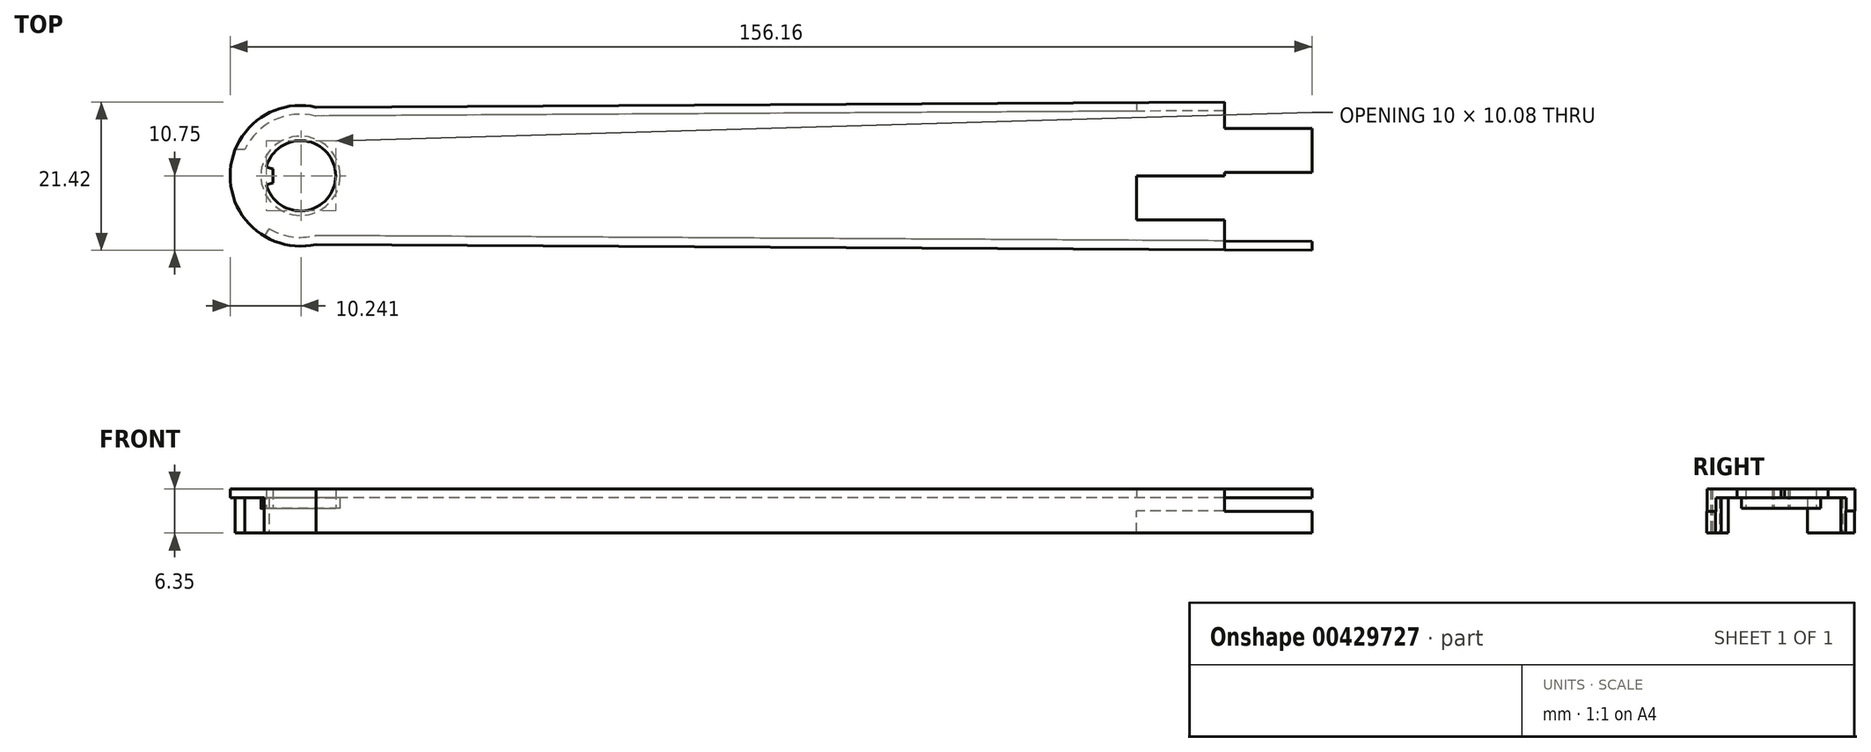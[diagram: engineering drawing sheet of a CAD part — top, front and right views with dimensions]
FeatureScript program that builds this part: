
annotation { "Feature Type Name" : "Feature", "Feature Type Description" : "" }
export const myFeature = defineFeature(function(context is Context, id is Id, definition is map)
    precondition{}
    {
        {
            var Q0;
            Q0=qCreatedBy(makeId("Top.planeOp"),FACE);
            var sketch = newSketch(context, id + "F0", { "sketchPlane" : qUnion([Q0])});
            skPoint(sketch, "E0", {"position": v(-133.35, 0) * mm});
            skPoint(sketch, "E1", {"position": v(133.35, 0) * mm});
            skCircle(sketch, "E2", {"center": v(-133.35, 0) * mm, "radius": 10.16 * mm});
            skCircle(sketch, "E3", {"center": v(133.35, 0) * mm, "radius": 12.07 * mm});
            skPoint(sketch, "E4", {"position": v(129.49, 11.43) * mm});
            skPoint(sketch, "E5", {"position": v(129.49, -11.43) * mm});
            skPoint(sketch, "E6", {"position": v(-131.1, 9.9) * mm});
            skPoint(sketch, "E7", {"position": v(-131.1, -9.9) * mm});
            skPoint(sketch, "E8", {"position": v(-133.35, 10.16) * mm});
            skPoint(sketch, "E9", {"position": v(133.35, 12.07) * mm});
            skLineSegment(sketch, "E10", {"start": v(129.49, 11.43) * mm, "end": v(-131.1, 9.9) * mm});
            skLineSegment(sketch, "E11", {"start": v(129.49, -11.43) * mm, "end": v(-131.1, -9.9) * mm});
            skLineSegment(sketch, "E12", {"start": v(0, 0) * mm, "end": v(0, -10.67) * mm});
            skLineSegment(sketch, "E13", {"start": v(0, 10.67) * mm, "end": v(0, 0) * mm});
            skSolve(sketch);
        }
        {
            var Q0;
            {var subQ0=sQuery(id+"F0.wireOp",EDGE,"E12");Q0=makeQuery(id+"F0.imprint","IMPRINT",FACE,{"disambiguationData":[TD([[makeQuery(id+"F0.imprint","IMPRINT",EDGE,{"derivedFrom":subQ0}),-1.0]])]});}
            var Q1;
            {var subQ0=sQuery(id+"F0.wireOp",EDGE,"E2");var subQ1=makeQuery(id+"F0.imprint","INTERSECT",VERTEX,{"derivedFrom":[subQ0,sQuery(id+"F0.wireOp",EDGE,"E10")]});Q1=makeQuery(id+"F0.imprint","IMPRINT",FACE,{"disambiguationData":[TD([[makeQuery(id+"F0.imprint","IMPRINT",EDGE,{"disambiguationData":[TD([[subQ1,-1.0]])],"derivedFrom":subQ0}),1.0]])]});}
            extrude(context, id + "F1", {"entities" : qUnion([Q0, Q1]), "depth" : 6.35 * mm});
        }
        {
            var Q0;
            Q0=makeQuery(id+"F1.opExtrude","CAP_FACE",FACE,{"disambiguationData":[OSD([sQuery(id+"F0.wireOp",EDGE,"E2"),sQuery(id+"F0.wireOp",EDGE,"E10"),sQuery(id+"F0.wireOp",EDGE,"E11"),sQuery(id+"F0.wireOp",EDGE,"E12"),sQuery(id+"F0.wireOp",EDGE,"E13")])],"isStart":true});
            var Q1;
            Q1=makeQuery(id+"F1.opExtrude","SWEPT_FACE",FACE,{"disambiguationData":[OSD([sQuery(id+"F0.wireOp",EDGE,"E12"),sQuery(id+"F0.wireOp",EDGE,"E13")])]});
            shell(context, id + "F2", {"entities" : qUnion([Q0, Q1]), "thickness" : 1.27 * mm});
        }
        {
            var Q0;
            Q0=makeQuery(id+"F2.opShell","OFFSET_FACE",FACE,{"disambiguationData":[OSD([sQuery(id+"F0.wireOp",EDGE,"E2"),sQuery(id+"F0.wireOp",EDGE,"E10"),sQuery(id+"F0.wireOp",EDGE,"E11"),sQuery(id+"F0.wireOp",EDGE,"ZJ3wcAUT-PQun-HVly-DXgm-6mWhBUt6tBkn"),sQuery(id+"F0.wireOp",EDGE,"E12")])]});
            var sketch = newSketch(context, id + "F3", { "sketchPlane" : qUnion([Q0])});
            skPoint(sketch, "E14", {"position": v(0, -0.5) * mm});
            skLineSegment(sketch, "E15.bottom", {"start": v(0, -0.5) * mm, "end": v(12.65, -0.5) * mm});
            skLineSegment(sketch, "E15.top", {"start": v(0, -6.8) * mm, "end": v(12.65, -6.8) * mm});
            skLineSegment(sketch, "E15.left", {"start": v(0, -0.5) * mm, "end": v(0, -6.8) * mm});
            skLineSegment(sketch, "E15.right", {"start": v(12.65, -0.5) * mm, "end": v(12.65, -6.8) * mm});
            skSolve(sketch);
        }
        {
            var Q0;
            Q0=makeQuery(id+"F3.imprint","IMPRINT",FACE,{"disambiguationData":[TD([[makeQuery(id+"F3.imprint","IMPRINT",EDGE,{"derivedFrom":sQuery(id+"F3.wireOp",EDGE,"E15.bottom")}),-1.0]])]});
            extrude(context, id + "F4", {"entities" : qUnion([Q0]), "oppositeDirection" : true, "depth" : 1.27 * mm});
        }
        {
            var Q0;
            Q0=makeQuery(id+"F4.opExtrude","SWEPT_BODY",BODY,{"disambiguationData":[OSD([sQuery(id+"F3.wireOp",EDGE,"E15.bottom"),sQuery(id+"F3.wireOp",EDGE,"E15.top"),sQuery(id+"F3.wireOp",EDGE,"E15.left"),sQuery(id+"F3.wireOp",EDGE,"E15.right")])]});
            var Q1;
            Q1=makeQuery(id+"F1.opExtrude","SWEPT_BODY",BODY,{"disambiguationData":[OSD([sQuery(id+"F0.wireOp",EDGE,"E2"),sQuery(id+"F0.wireOp",EDGE,"E10"),sQuery(id+"F0.wireOp",EDGE,"E11"),sQuery(id+"F0.wireOp",EDGE,"ZJ3wcAUT-PQun-HVly-DXgm-6mWhBUt6tBkn"),sQuery(id+"F0.wireOp",EDGE,"E12")])]});
            booleanBodies(context, id + "F5", {"operationType" : BooleanOperationType.UNION, "tools" : qUnion([Q0, Q1])});
        }
        {
            var Q0;
            Q0=makeQuery(id+"F2.opShell","OFFSET_FACE",FACE,{"disambiguationData":[OSD([sQuery(id+"F0.wireOp",EDGE,"E11")])]});
            var sketch = newSketch(context, id + "F6", { "sketchPlane" : qUnion([Q0])});
            skLineSegment(sketch, "E16.bottom", {"start": v(0, 0) * mm, "end": v(-12.7, 0) * mm});
            skLineSegment(sketch, "E16.top", {"start": v(0, 3.12) * mm, "end": v(-12.7, 3.12) * mm});
            skLineSegment(sketch, "E16.left", {"start": v(0, 0) * mm, "end": v(0, 3.12) * mm});
            skLineSegment(sketch, "E16.right", {"start": v(-12.7, 0) * mm, "end": v(-12.7, 3.12) * mm});
            skSolve(sketch);
        }
        {
            var Q0;
            {var subQ3=sQuery(id+"F6.wireOp",EDGE,"E16.right");Q0=makeQuery(id+"F6.imprint","IMPRINT",FACE,{"disambiguationData":[TD([[makeQuery(id+"F6.imprint","IMPRINT",EDGE,{"derivedFrom":subQ3}),-1.0]])]});}
            extrude(context, id + "F7", {"entities" : qUnion([Q0]), "operationType" : NewBodyOperationType.ADD, "oppositeDirection" : true, "depth" : 1.27 * mm});
        }
        {
            var Q0;
            Q0=makeQuery(id+"F2.opShell","OFFSET_FACE",FACE,{"disambiguationData":[OSD([sQuery(id+"F0.wireOp",EDGE,"E10")])]});
            var sketch = newSketch(context, id + "F8", { "sketchPlane" : qUnion([Q0])});
            skPoint(sketch, "E17", {"position": v(1.32, 0) * mm});
            skLineSegment(sketch, "E18.bottom", {"start": v(1.32, 0) * mm, "end": v(-12.65, 0) * mm});
            skLineSegment(sketch, "E18.top", {"start": v(1.32, 3.18) * mm, "end": v(-12.65, 3.17) * mm});
            skLineSegment(sketch, "E18.left", {"start": v(1.32, 0) * mm, "end": v(1.32, 3.18) * mm});
            skLineSegment(sketch, "E18.right", {"start": v(-12.65, 0) * mm, "end": v(-12.65, 3.17) * mm});
            skSolve(sketch);
        }
        {
            var Q0;
            {var subQ4=sQuery(id+"F8.wireOp",EDGE,"E18.right");Q0=makeQuery(id+"F8.imprint","IMPRINT",FACE,{"disambiguationData":[TD([[makeQuery(id+"F8.imprint","IMPRINT",EDGE,{"derivedFrom":subQ4}),-1.0]])]});}
            var Q1;
            {var subQ3=sQuery(id+"F8.wireOp",EDGE,"E18.left");Q1=makeQuery(id+"F8.imprint","IMPRINT",FACE,{"disambiguationData":[TD([[makeQuery(id+"F8.imprint","IMPRINT",EDGE,{"derivedFrom":subQ3}),1.0]])]});}
            extrude(context, id + "F9", {"entities" : qUnion([Q0, Q1]), "operationType" : NewBodyOperationType.REMOVE, "oppositeDirection" : true, "depth" : 25.4 * mm});
        }
        {
            var Q0;
            Q0=makeQuery(id+"F5.opBoolean","MERGE",FACE,{"derivedFrom":[makeQuery(id+"F2.opShell","OFFSET_FACE",FACE,{"disambiguationData":[OSD([sQuery(id+"F0.wireOp",EDGE,"E2"),sQuery(id+"F0.wireOp",EDGE,"E10"),sQuery(id+"F0.wireOp",EDGE,"E11"),sQuery(id+"F0.wireOp",EDGE,"E12"),sQuery(id+"F0.wireOp",EDGE,"E13")])]}),makeQuery(id+"F4.opExtrude","CAP_FACE",FACE,{"disambiguationData":[OSD([sQuery(id+"F3.wireOp",EDGE,"E15.bottom"),sQuery(id+"F3.wireOp",EDGE,"E15.top"),sQuery(id+"F3.wireOp",EDGE,"E15.left"),sQuery(id+"F3.wireOp",EDGE,"E15.right")])],"isStart":true})]});
            var sketch = newSketch(context, id + "F10", { "sketchPlane" : qUnion([Q0])});
            skCircle(sketch, "E19", {"center": v(-133.35, 0) * mm, "radius": 5.72 * mm});
            skSolve(sketch);
        }
        {
            var Q0;
            Q0=makeQuery(id+"F10.imprint","IMPRINT",FACE,{"disambiguationData":[TD([[makeQuery(id+"F10.imprint","IMPRINT",EDGE,{"derivedFrom":sQuery(id+"F10.wireOp",EDGE,"E19")}),1.0]])]});
            extrude(context, id + "F11", {"entities" : qUnion([Q0]), "operationType" : NewBodyOperationType.ADD, "depth" : 1.52 * mm});
        }
        {
            var Q0;
            Q0=makeQuery(id+"F11.opExtrude","CAP_FACE",FACE,{"disambiguationData":[OSD([sQuery(id+"F10.wireOp",EDGE,"E19")])],"isStart":false});
            var sketch = newSketch(context, id + "F12", { "sketchPlane" : qUnion([Q0])});
            skCircle(sketch, "E20", {"center": v(-133.35, 0) * mm, "radius": 5.08 * mm});
            skPoint(sketch, "E21", {"position": v(-138.27, 1.27) * mm});
            skPoint(sketch, "E22", {"position": v(-138.27, -1.27) * mm});
            skPoint(sketch, "E23", {"position": v(-137.31, 1.02) * mm});
            skPoint(sketch, "E24", {"position": v(-137.31, -1.02) * mm});
            skPoint(sketch, "E25", {"position": v(-139.07, 0) * mm});
            skLineSegment(sketch, "E26", {"start": v(-138.27, 1.27) * mm, "end": v(-137.31, 1.02) * mm});
            skLineSegment(sketch, "E27", {"start": v(-137.31, -1.02) * mm, "end": v(-137.31, 1.02) * mm});
            skLineSegment(sketch, "E28", {"start": v(-137.31, -1.02) * mm, "end": v(-138.27, -1.27) * mm});
            skSolve(sketch);
        }
        {
            var Q0;
            {var subQ0=sQuery(id+"F12.wireOp",EDGE,"E26");Q0=makeQuery(id+"F12.imprint","IMPRINT",FACE,{"disambiguationData":[TD([[makeQuery(id+"F12.imprint","IMPRINT",EDGE,{"derivedFrom":subQ0}),1.0]])]});}
            extrude(context, id + "F13", {"entities" : qUnion([Q0]), "operationType" : NewBodyOperationType.REMOVE, "oppositeDirection" : true, "depth" : 25.4 * mm});
        }
        {
            var Q0;
            Q0=makeQuery(id+"F7.boolean.opBoolean","MERGE",FACE,{"derivedFrom":[makeQuery(id+"F1.opExtrude","CAP_FACE",FACE,{"disambiguationData":[OSD([sQuery(id+"F0.wireOp",EDGE,"E2"),sQuery(id+"F0.wireOp",EDGE,"E10"),sQuery(id+"F0.wireOp",EDGE,"E11"),sQuery(id+"F0.wireOp",EDGE,"E12"),sQuery(id+"F0.wireOp",EDGE,"E13")])],"isStart":true}),makeQuery(id+"F7.opExtrude","SWEPT_FACE",FACE,{"disambiguationData":[OSD([sQuery(id+"F6.wireOp",EDGE,"E16.bottom")])]})]});
            var sketch = newSketch(context, id + "F14", { "sketchPlane" : qUnion([Q0])});
            skPoint(sketch, "E29", {"position": v(-141.38, -3.81) * mm});
            skPoint(sketch, "E30", {"position": v(-137.93, 7.62) * mm});
            skPoint(sketch, "E31", {"position": v(-133.35, 0) * mm});
            skPoint(sketch, "E32", {"position": v(-138.58, 8.7) * mm});
            skPoint(sketch, "E33", {"position": v(-142.77, -3.81) * mm});
            skLineSegment(sketch, "E34", {"start": v(-138.58, 8.7) * mm, "end": v(-133.35, 0) * mm});
            skLineSegment(sketch, "E35", {"start": v(-142.77, -3.81) * mm, "end": v(-141.38, -3.81) * mm});
            skArc(sketch, "E36", {"start": v(-137.93, 7.62) * mm, "mid": v(-141.86, 2.57) * mm, "end": v(-141.38, -3.8) * mm});
            skArc(sketch, "E37", {"start": v(-138.58, 8.7) * mm, "mid": v(-142.99, 3.22) * mm, "end": v(-142.77, -3.81) * mm});
            skSolve(sketch);
        }
        {
            var Q0;
            Q0=makeQuery(id+"F14.imprint","IMPRINT",FACE,{"disambiguationData":[TD([[makeQuery(id+"F14.imprint","IMPRINT",EDGE,{"derivedFrom":sQuery(id+"F14.wireOp",EDGE,"E35")}),1.0]])]});
            var Q1;
            Q1=makeQuery(id+"F5.opBoolean","MERGE",FACE,{"derivedFrom":[makeQuery(id+"F2.opShell","OFFSET_FACE",FACE,{"disambiguationData":[OSD([sQuery(id+"F0.wireOp",EDGE,"E2"),sQuery(id+"F0.wireOp",EDGE,"E10"),sQuery(id+"F0.wireOp",EDGE,"E11"),sQuery(id+"F0.wireOp",EDGE,"E12"),sQuery(id+"F0.wireOp",EDGE,"E13")])]}),makeQuery(id+"F4.opExtrude","CAP_FACE",FACE,{"disambiguationData":[OSD([sQuery(id+"F3.wireOp",EDGE,"E15.bottom"),sQuery(id+"F3.wireOp",EDGE,"E15.top"),sQuery(id+"F3.wireOp",EDGE,"E15.left"),sQuery(id+"F3.wireOp",EDGE,"E15.right")])],"isStart":true})]});
            extrude(context, id + "F15", {"entities" : qUnion([Q0]), "operationType" : NewBodyOperationType.REMOVE, "endBound" : BoundingType.UP_TO_SURFACE, "oppositeDirection" : true, "endBoundEntityFace" : qUnion([Q1]), "depth" : 25.4 * mm});
        }
        {
            var Q0;
            {var subQ0=sQuery(id+"F3.wireOp",EDGE,"E15.right");var subQ1=sQuery(id+"F3.wireOp",EDGE,"E15.left");var subQ2=sQuery(id+"F3.wireOp",EDGE,"E15.top");var subQ3=sQuery(id+"F3.wireOp",EDGE,"E15.bottom");var subQ4=sQuery(id+"F0.wireOp",EDGE,"E13");var subQ5=sQuery(id+"F0.wireOp",EDGE,"E12");var subQ6=sQuery(id+"F0.wireOp",EDGE,"E11");var subQ7=sQuery(id+"F0.wireOp",EDGE,"E10");var subQ8=sQuery(id+"F0.wireOp",EDGE,"E2");Q0=makeQuery(id+"F15.boolean.opBoolean","MERGE",FACE,{"derivedFrom":[makeQuery(id+"F5.opBoolean","MERGE",FACE,{"derivedFrom":[makeQuery(id+"F2.opShell","OFFSET_FACE",FACE,{"disambiguationData":[OSD([subQ8,subQ7,subQ6,subQ5,subQ4])]}),makeQuery(id+"F4.opExtrude","CAP_FACE",FACE,{"disambiguationData":[OSD([subQ3,subQ2,subQ1,subQ0])],"isStart":true})]}),makeQuery(id+"F15.opExtrude","CAP_FACE",FACE,{"disambiguationData":[OSD([subQ8,subQ7,subQ6,subQ5,subQ4,subQ3,subQ2,subQ1,subQ0])],"isStart":false})]});}
            var sketch = newSketch(context, id + "F16", { "sketchPlane" : qUnion([Q0])});
            skLineSegment(sketch, "E38.bottom", {"start": v(0, 0) * mm, "end": v(-12.7, 0) * mm});
            skLineSegment(sketch, "E38.top", {"start": v(0, 6.35) * mm, "end": v(-12.7, 6.35) * mm});
            skLineSegment(sketch, "E38.left", {"start": v(0, 0) * mm, "end": v(0, 6.35) * mm});
            skLineSegment(sketch, "E38.right", {"start": v(-12.7, 0) * mm, "end": v(-12.7, 6.35) * mm});
            skSolve(sketch);
        }
        {
            var Q0;
            Q0=makeQuery(id+"F16.imprint","IMPRINT",FACE,{"disambiguationData":[TD([[makeQuery(id+"F16.imprint","IMPRINT",EDGE,{"derivedFrom":sQuery(id+"F16.wireOp",EDGE,"E38.bottom")}),-1.0]])]});
            extrude(context, id + "F17", {"entities" : qUnion([Q0]), "operationType" : NewBodyOperationType.REMOVE, "oppositeDirection" : true, "depth" : 25.4 * mm});
        }
    });
